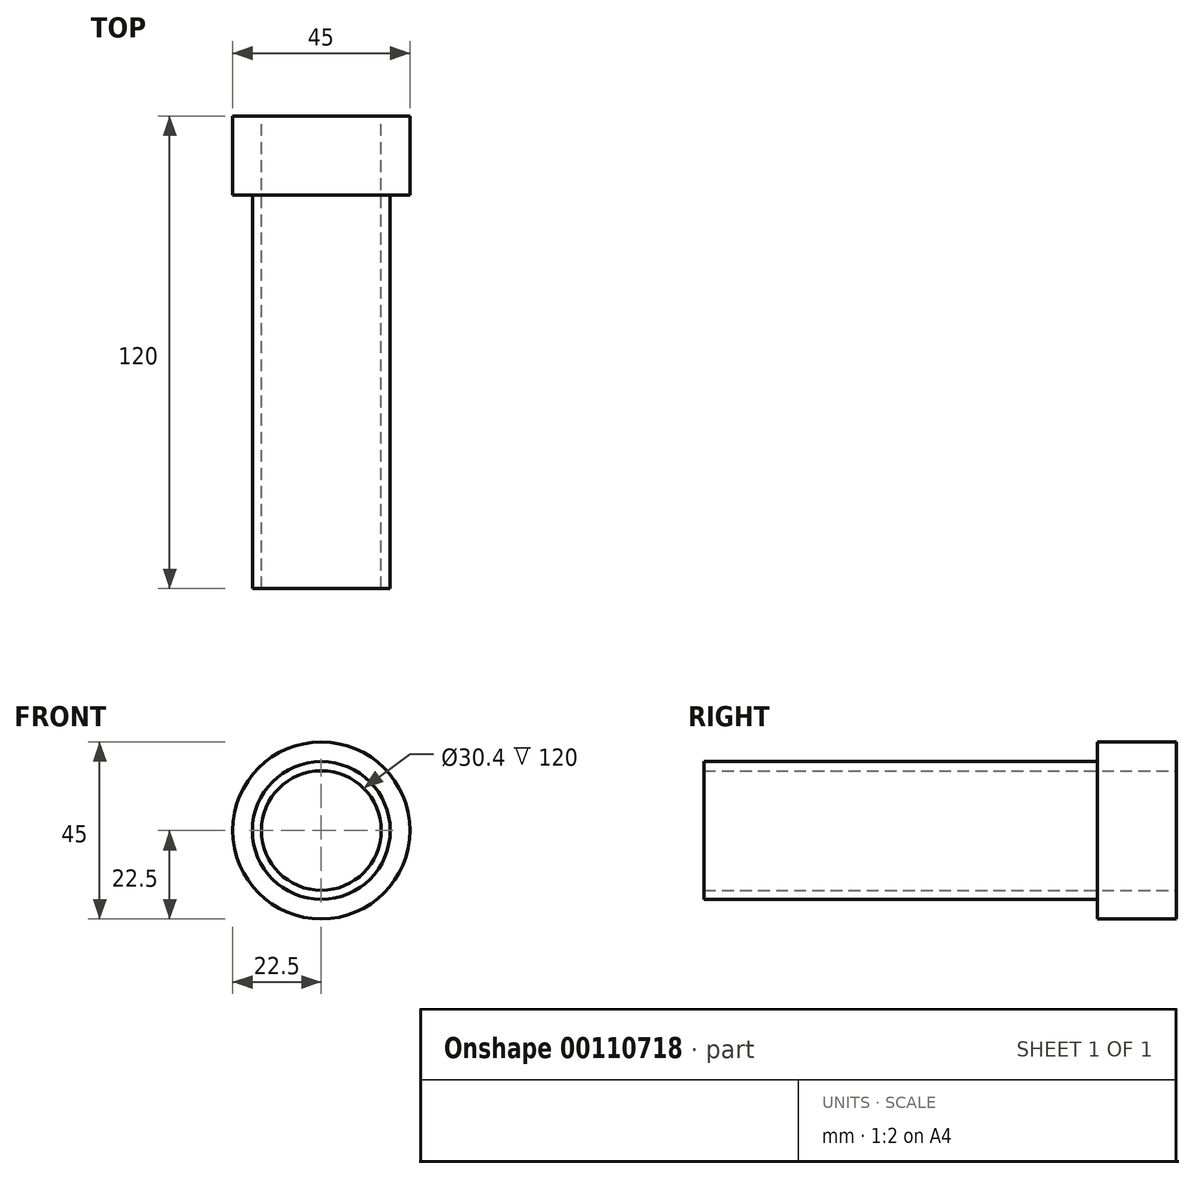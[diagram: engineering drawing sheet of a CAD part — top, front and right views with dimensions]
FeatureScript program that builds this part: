
annotation { "Feature Type Name" : "Feature", "Feature Type Description" : "" }
export const myFeature = defineFeature(function(context is Context, id is Id, definition is map)
    precondition{}
    {
        {
            var Q0;
            Q0=qCreatedBy(makeId("Front.planeOp"),FACE);
            var sketch = newSketch(context, id + "F0", { "sketchPlane" : qUnion([Q0])});
            skCircle(sketch, "E0", {"center": v(0, 0) * mm, "radius": 22.5 * mm});
            skCircle(sketch, "E1", {"center": v(0, 0) * mm, "radius": 17.5 * mm});
            skCircle(sketch, "E2", {"center": v(0, 0) * mm, "radius": 15.2 * mm});
            skSolve(sketch);
        }
        {
            var Q0;
            Q0=makeQuery(id+"F0.imprint","IMPRINT",FACE,{"disambiguationData":[TD([[makeQuery(id+"F0.imprint","IMPRINT",EDGE,{"derivedFrom":sQuery(id+"F0.wireOp",EDGE,"E1")}),1.0]])]});
            var Q1;
            Q1=makeQuery(id+"F0.imprint","IMPRINT",FACE,{"disambiguationData":[TD([[makeQuery(id+"F0.imprint","IMPRINT",EDGE,{"derivedFrom":sQuery(id+"F0.wireOp",EDGE,"E0")}),1.0]])]});
            extrude(context, id + "F1", {"entities" : qUnion([Q0, Q1]), "depth" : 20 * mm});
        }
        {
            var Q0;
            Q0=makeQuery(id+"F0.imprint","IMPRINT",FACE,{"disambiguationData":[TD([[makeQuery(id+"F0.imprint","IMPRINT",EDGE,{"derivedFrom":sQuery(id+"F0.wireOp",EDGE,"E1")}),1.0]])]});
            extrude(context, id + "F2", {"entities" : qUnion([Q0]), "operationType" : NewBodyOperationType.ADD, "depth" : 120 * mm});
        }
    });
